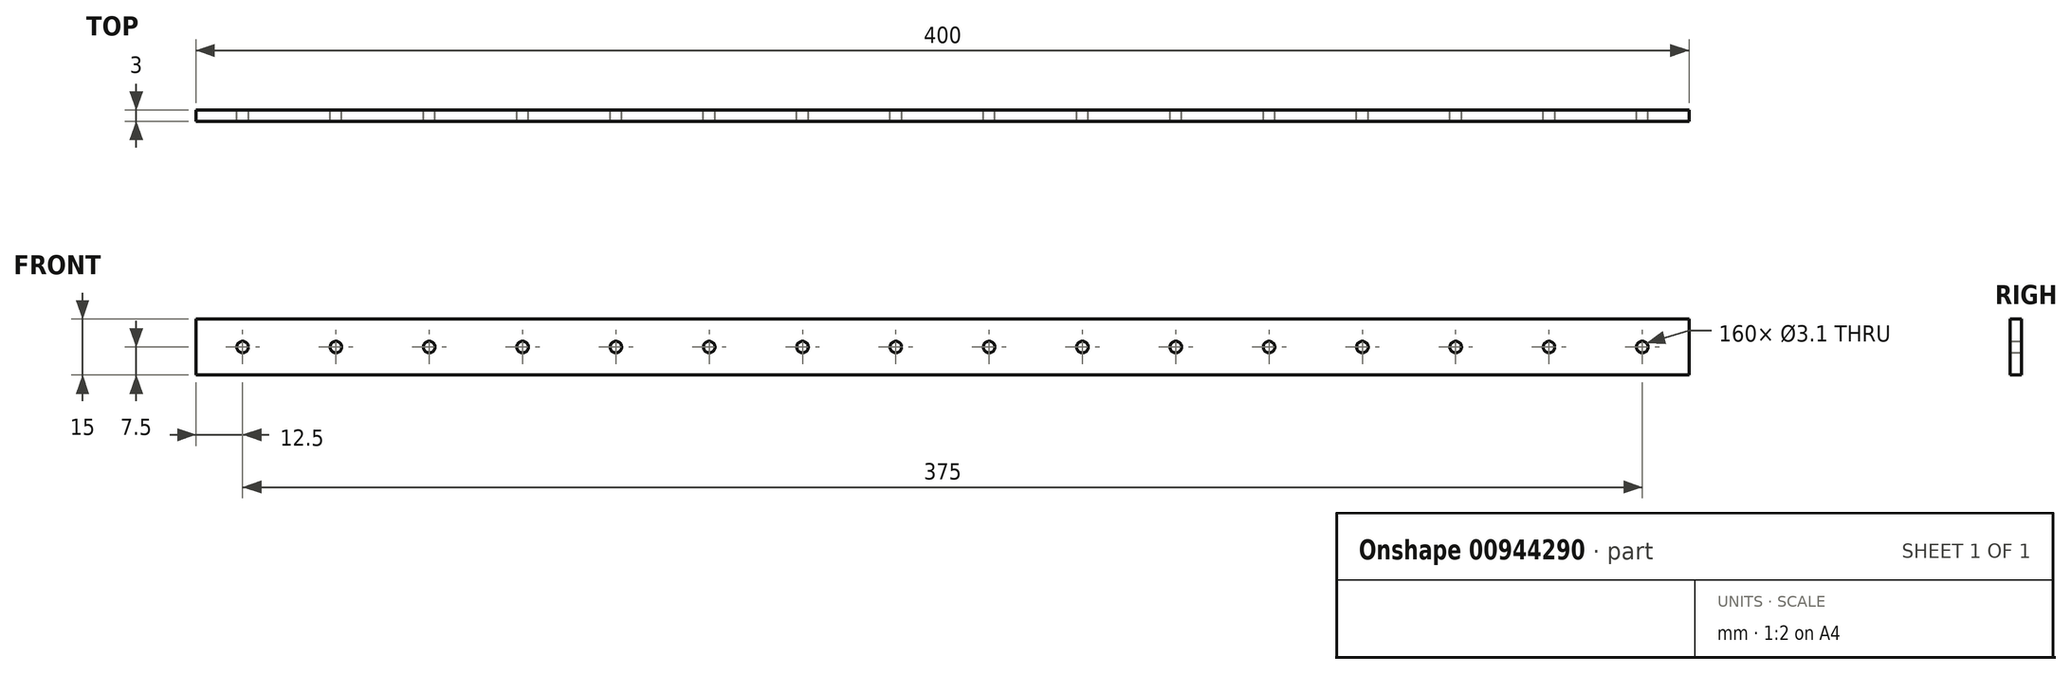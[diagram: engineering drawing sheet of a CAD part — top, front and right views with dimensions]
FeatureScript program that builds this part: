
annotation { "Feature Type Name" : "Feature", "Feature Type Description" : "" }
export const myFeature = defineFeature(function(context is Context, id is Id, definition is map)
    precondition{}
    {
        {
            var Q0;
            Q0=qCreatedBy(makeId("Front.planeOp"),FACE);
            var sketch = newSketch(context, id + "F0", { "sketchPlane" : qUnion([Q0])});
            skLineSegment(sketch, "E0.bottom", {"start": v(200, 7.5) * mm, "end": v(-200, 7.5) * mm});
            skLineSegment(sketch, "E0.top", {"start": v(200, -7.5) * mm, "end": v(-200, -7.5) * mm});
            skLineSegment(sketch, "E0.left", {"start": v(200, 7.5) * mm, "end": v(200, -7.5) * mm});
            skLineSegment(sketch, "E0.right", {"start": v(-200, 7.5) * mm, "end": v(-200, -7.5) * mm});
            skPoint(sketch, "E0.middle", {"position": v(0, 0) * mm});
            skLineSegment(sketch, "E1", {"start": v(-200, 0) * mm, "end": v(200, 0) * mm, "construction": true});
            skCircle(sketch, "E2", {"center": v(-187.5, 0) * mm, "radius": 1.55 * mm});
            skCircle(sketch, "E3.1.0.0", {"center": v(-162.5, 0) * mm, "radius": 1.55 * mm});
            skCircle(sketch, "E3.2.0.0", {"center": v(-137.5, 0) * mm, "radius": 1.55 * mm});
            skCircle(sketch, "E3.3.0.0", {"center": v(-112.5, 0) * mm, "radius": 1.55 * mm});
            skCircle(sketch, "E3.4.0.0", {"center": v(-87.5, 0) * mm, "radius": 1.55 * mm});
            skCircle(sketch, "E3.5.0.0", {"center": v(-62.5, 0) * mm, "radius": 1.55 * mm});
            skCircle(sketch, "E3.6.0.0", {"center": v(-37.5, 0) * mm, "radius": 1.55 * mm});
            skCircle(sketch, "E3.7.0.0", {"center": v(-12.5, 0) * mm, "radius": 1.55 * mm});
            skCircle(sketch, "E3.8.0.0", {"center": v(12.5, 0) * mm, "radius": 1.55 * mm});
            skCircle(sketch, "E3.9.0.0", {"center": v(37.5, 0) * mm, "radius": 1.55 * mm});
            skCircle(sketch, "E3.10.0.0", {"center": v(62.5, 0) * mm, "radius": 1.55 * mm});
            skCircle(sketch, "E3.11.0.0", {"center": v(87.5, 0) * mm, "radius": 1.55 * mm});
            skCircle(sketch, "E3.12.0.0", {"center": v(112.5, 0) * mm, "radius": 1.55 * mm});
            skCircle(sketch, "E3.13.0.0", {"center": v(137.5, 0) * mm, "radius": 1.55 * mm});
            skCircle(sketch, "E3.14.0.0", {"center": v(162.5, 0) * mm, "radius": 1.55 * mm});
            skCircle(sketch, "E3.15.0.0", {"center": v(187.5, 0) * mm, "radius": 1.55 * mm});
            skLineSegment(sketch, "E3.direction1", {"start": v(-187.5, 0) * mm, "end": v(-162.5, 0) * mm, "construction": true});
            skSolve(sketch);
        }
        {
            var Q0;
            Q0=qSketchRegion(id+"F0",true);
            extrude(context, id + "F1", {"entities" : qUnion([Q0]), "depth" : 3 * mm, "offsetDistance" : 25 * mm});
        }
    });
